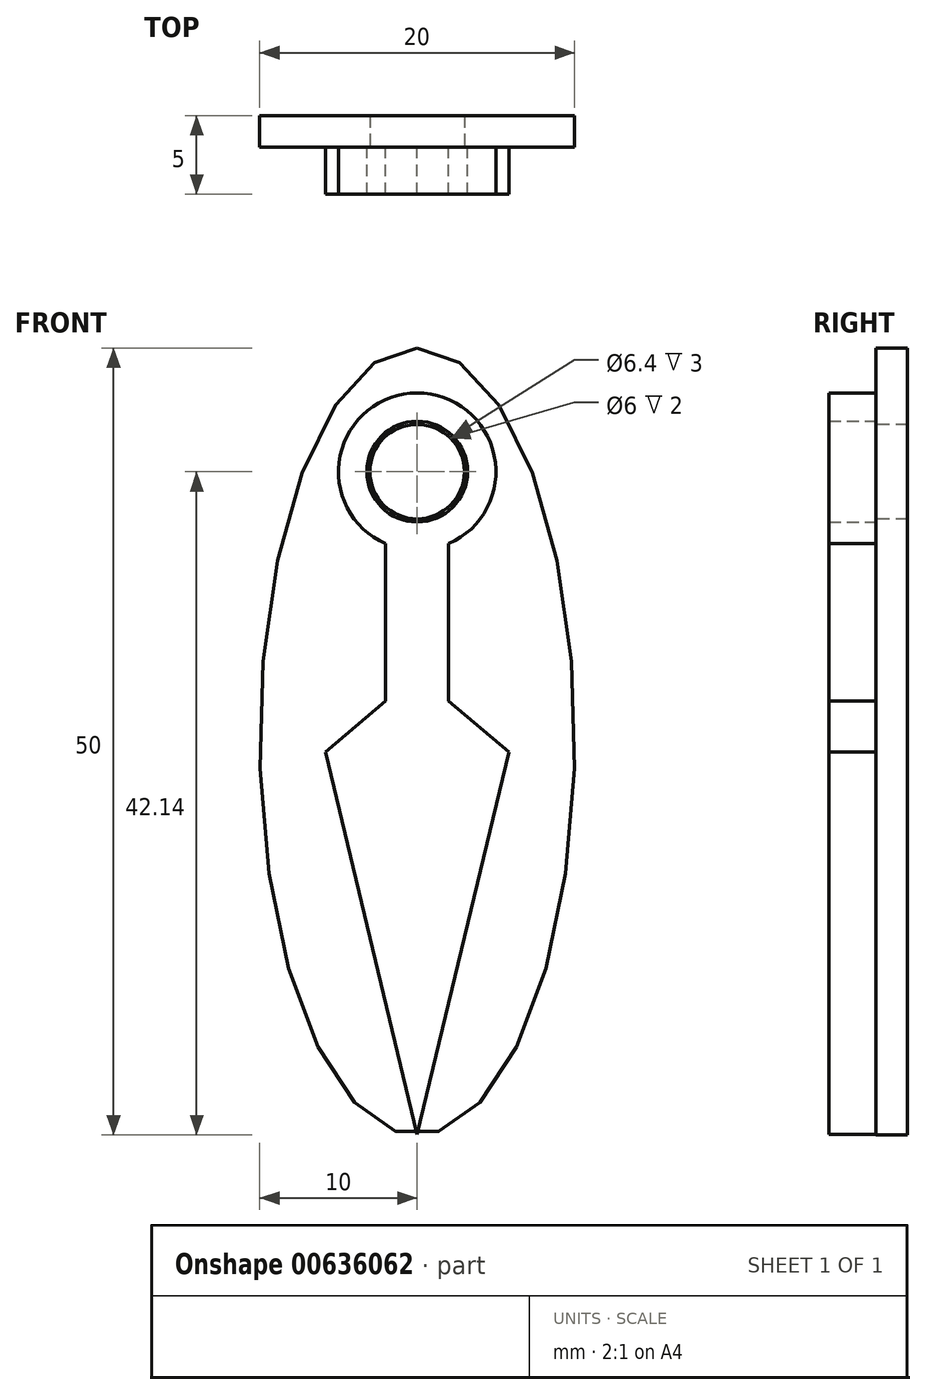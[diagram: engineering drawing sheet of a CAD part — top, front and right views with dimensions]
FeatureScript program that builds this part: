
annotation { "Feature Type Name" : "Feature", "Feature Type Description" : "" }
export const myFeature = defineFeature(function(context is Context, id is Id, definition is map)
    precondition{}
    {
        {
            var Q0;
            Q0=qCreatedBy(makeId("Front.planeOp"),FACE);
            var sketch = newSketch(context, id + "F0", { "sketchPlane" : qUnion([Q0])});
            skCircle(sketch, "E0", {"center": v(0, 0) * mm, "radius": 5 * mm});
            skCircle(sketch, "E1", {"center": v(0, 0) * mm, "radius": 3.2 * mm});
            skLineSegment(sketch, "E2", {"start": v(-2, -4.58) * mm, "end": v(-2, -14.58) * mm});
            skLineSegment(sketch, "E3", {"start": v(2, -4.58) * mm, "end": v(2, -14.58) * mm});
            skLineSegment(sketch, "E4", {"start": v(2, -14.58) * mm, "end": v(5.83, -17.8) * mm});
            skLineSegment(sketch, "E5", {"start": v(-2, -14.58) * mm, "end": v(-5.83, -17.8) * mm});
            skLineSegment(sketch, "E6", {"start": v(5.83, -17.8) * mm, "end": v(0, -42.1) * mm});
            skLineSegment(sketch, "E7", {"start": v(0, -42.1) * mm, "end": v(-5.83, -17.8) * mm});
            skLineSegment(sketch, "E8", {"start": v(-2, -14.58) * mm, "end": v(2, -14.58) * mm});
            skSolve(sketch);
        }
        {
            var Q0;
            Q0=makeQuery(id+"F0.imprint","IMPRINT",FACE,{"disambiguationData":[TD([[makeQuery(id+"F0.imprint","IMPRINT",EDGE,{"derivedFrom":sQuery(id+"F0.wireOp",EDGE,"E4")}),-1.0]])]});
            var Q1;
            {var subQ0=sQuery(id+"F0.wireOp",EDGE,"E2");Q1=makeQuery(id+"F0.imprint","IMPRINT",FACE,{"disambiguationData":[TD([[makeQuery(id+"F0.imprint","IMPRINT",EDGE,{"derivedFrom":subQ0}),1.0]])]});}
            var Q2;
            Q2=makeQuery(id+"F0.imprint","IMPRINT",FACE,{"disambiguationData":[TD([[makeQuery(id+"F0.imprint","IMPRINT",EDGE,{"derivedFrom":sQuery(id+"F0.wireOp",EDGE,"E1")}),-1.0]])]});
            extrude(context, id + "F1", {"entities" : qUnion([Q0, Q1, Q2]), "depth" : 5 * mm, "offsetDistance" : 25 * mm});
        }
        {
            var Q0;
            Q0=qCreatedBy(makeId("Front.planeOp"),FACE);
            var sketch = newSketch(context, id + "F2", { "sketchPlane" : qUnion([Q0])});
            skEllipse(sketch, "E9", {"center": v(0, -17.14) * mm, "majorRadius": 25 * mm, "minorRadius": 10 * mm, "majorAxis": v(0, 1)});
            skSolve(sketch);
        }
        {
            var Q0;
            Q0 = qSketchRegion(id + "F2", true);
            extrude(context, id + "F3", {"entities" : qUnion([Q0]), "operationType" : NewBodyOperationType.ADD, "depth" : 2 * mm, "offsetDistance" : 25 * mm});
        }
        {
            var Q0;
            Q0=makeQuery(id+"F3.boolean.opBoolean","SPLIT",FACE,{"disambiguationData":[TD([makeQuery(id+"F1.opExtrude","SWEPT_FACE",FACE,{"disambiguationData":[OSD([sQuery(id+"F0.wireOp",EDGE,"E1")])]})])],"derivedFrom":makeQuery(id+"F3.opExtrude","CAP_FACE",FACE,{"disambiguationData":[OSD([sQuery(id+"F2.wireOp",EDGE,"E9")])],"isStart":false})});
            var sketch = newSketch(context, id + "F4", { "sketchPlane" : qUnion([Q0])});
            skCircle(sketch, "E10", {"center": v(0, 0) * mm, "radius": 3 * mm});
            skSolve(sketch);
        }
        {
            var Q0;
            Q0 = qSketchRegion(id + "F4", true);
            extrude(context, id + "F5", {"entities" : qUnion([Q0]), "operationType" : NewBodyOperationType.REMOVE, "oppositeDirection" : true, "depth" : 5 * mm, "offsetDistance" : 25 * mm});
        }
    });
